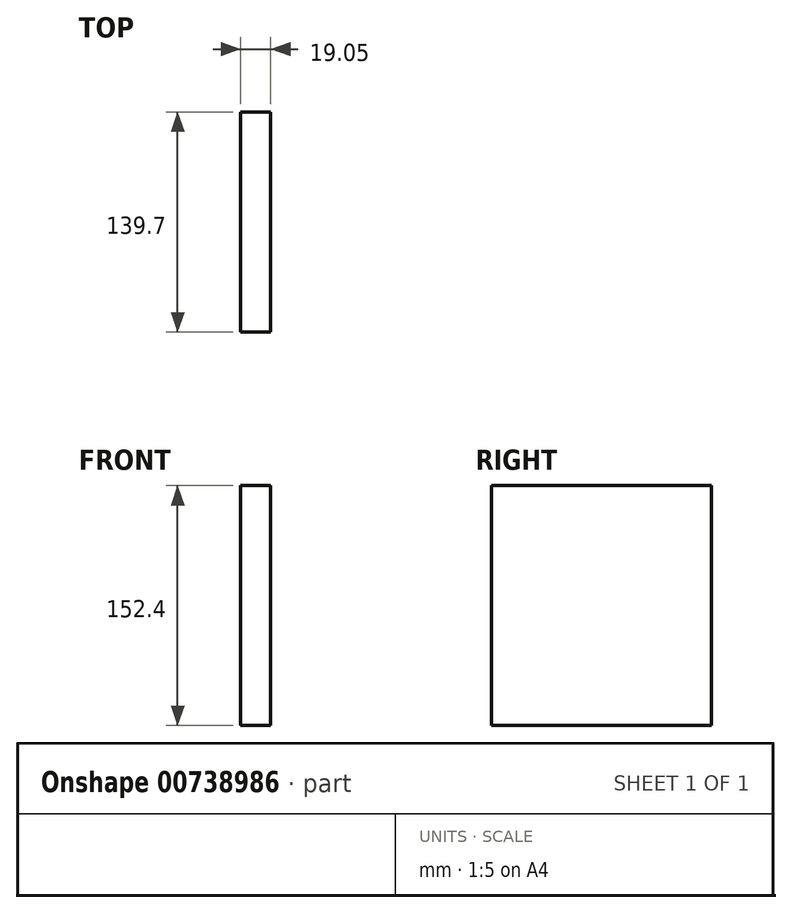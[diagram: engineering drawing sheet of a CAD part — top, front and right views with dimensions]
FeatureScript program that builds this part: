
annotation { "Feature Type Name" : "Feature", "Feature Type Description" : "" }
export const myFeature = defineFeature(function(context is Context, id is Id, definition is map)
    precondition{}
    {
        {
            var Q0;
            Q0=qCreatedBy(makeId("Right.planeOp"),FACE);
            var sketch = newSketch(context, id + "F0", { "sketchPlane" : qUnion([Q0])});
            skLineSegment(sketch, "E0.bottom", {"start": v(-139.7, 0) * mm, "end": v(0, 0) * mm});
            skLineSegment(sketch, "E0.top", {"start": v(-139.7, -152.4) * mm, "end": v(0, -152.4) * mm});
            skLineSegment(sketch, "E0.left", {"start": v(-139.7, 0) * mm, "end": v(-139.7, -152.4) * mm});
            skLineSegment(sketch, "E0.right", {"start": v(0, 0) * mm, "end": v(0, -152.4) * mm});
            skSolve(sketch);
        }
        {
            var Q0;
            Q0=qSketchRegion(id+"F0",true);
            extrude(context, id + "F1", {"entities" : qUnion([Q0]), "depth" : 19.05 * mm, "offsetDistance" : 25.4 * mm});
        }
    });
